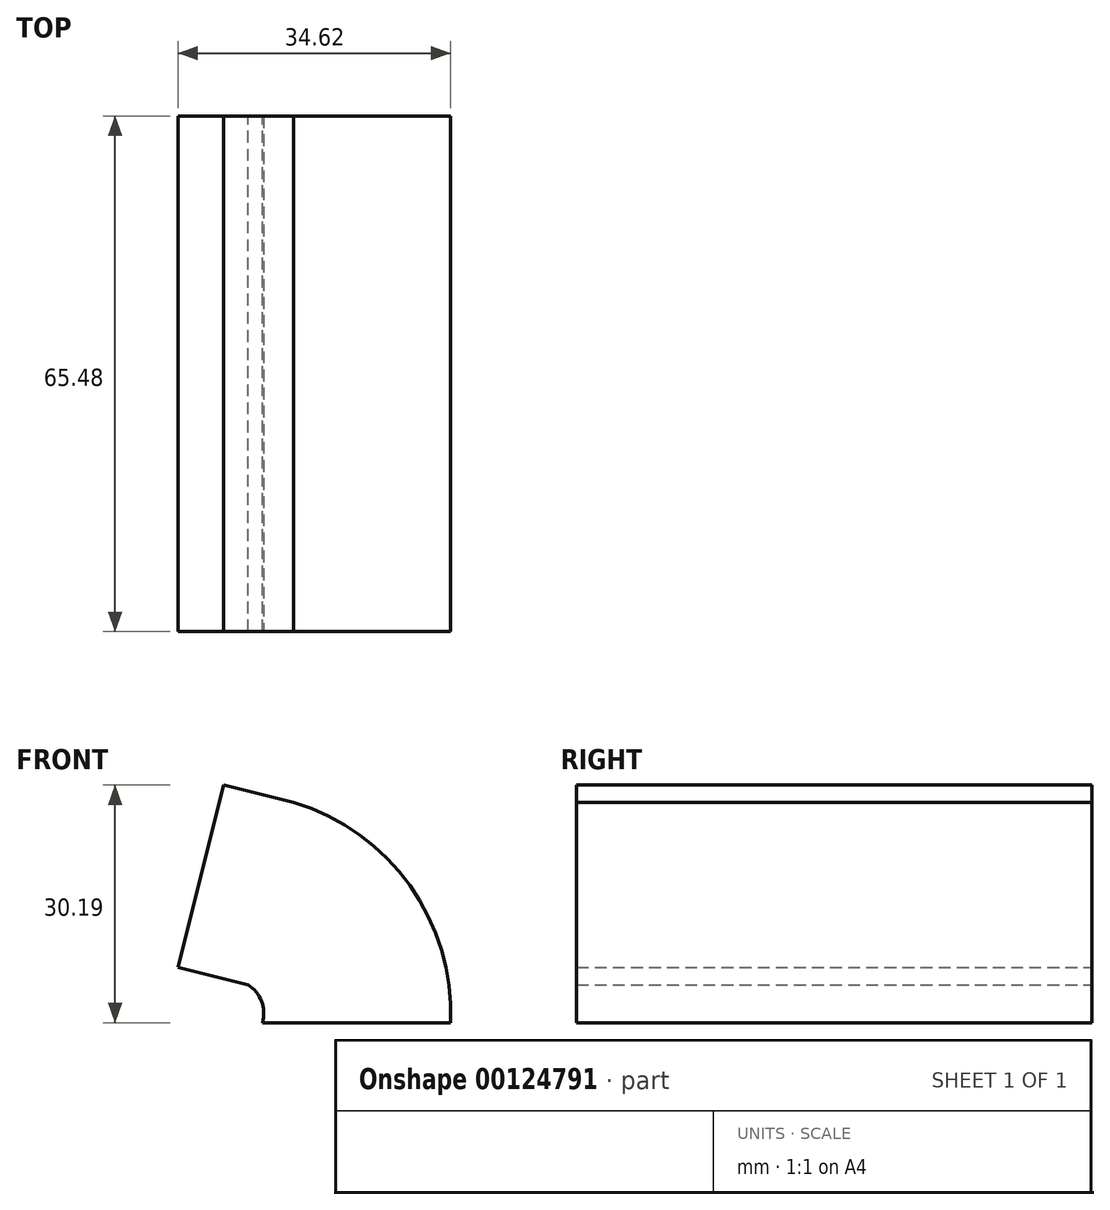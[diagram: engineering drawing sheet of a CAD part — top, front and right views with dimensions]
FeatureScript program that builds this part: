
annotation { "Feature Type Name" : "Feature", "Feature Type Description" : "" }
export const myFeature = defineFeature(function(context is Context, id is Id, definition is map)
    precondition{}
    {
        {
            var Q0;
            Q0=qCreatedBy(makeId("Front.planeOp"),FACE);
            var sketch = newSketch(context, id + "F0", { "sketchPlane" : qUnion([Q0])});
            skArc(sketch, "E0", {"start": v(0, 0) * mm, "mid": v(-5.15, 17.41) * mm, "end": v(-19.92, 27.97) * mm});
            skSolve(sketch);
        }
        {
            var Q0;
            Q0=qCreatedBy(makeId("Top.planeOp"),FACE);
            var sketch = newSketch(context, id + "F1", { "sketchPlane" : qUnion([Q0])});
            skLineSegment(sketch, "E1.bottom", {"start": v(0, -16.46) * mm, "end": v(-23.89, -16.46) * mm});
            skLineSegment(sketch, "E1.top", {"start": v(0, 49.02) * mm, "end": v(-23.89, 49.02) * mm});
            skLineSegment(sketch, "E1.left", {"start": v(0, -16.46) * mm, "end": v(0, 49.02) * mm});
            skLineSegment(sketch, "E1.right", {"start": v(-23.89, -16.46) * mm, "end": v(-23.89, 49.02) * mm});
            skSolve(sketch);
        }
        {
            var Q0;
            Q0=makeQuery(id+"F1.imprint","IMPRINT",FACE,{"disambiguationData":[TD([[makeQuery(id+"F1.imprint","IMPRINT",EDGE,{"derivedFrom":sQuery(id+"F1.wireOp",EDGE,"E1.bottom")}),-1.0]])]});
            var Q1;
            Q1=sQuery(id+"F0.wireOp",EDGE,"E0");
            sweep(context, id + "F2", {"profiles" : qUnion([Q0]), "path" : qUnion([Q1])});
        }
        {
            var Q0;
            Q0=makeQuery(id+"F2.opSweep","CAP_FACE",FACE,{"disambiguationData":[OSD([sQuery(id+"F0.wireOp",VERTEX,"E0.end"),sQuery(id+"F1.wireOp",EDGE,"E1.bottom"),sQuery(id+"F1.wireOp",EDGE,"E1.top"),sQuery(id+"F1.wireOp",EDGE,"E1.left"),sQuery(id+"F1.wireOp",EDGE,"E1.right")])],"isStart":false});
            extrude(context, id + "F3", {"entities" : qUnion([Q0]), "operationType" : NewBodyOperationType.ADD, "depth" : 9.14 * mm});
        }
    });
